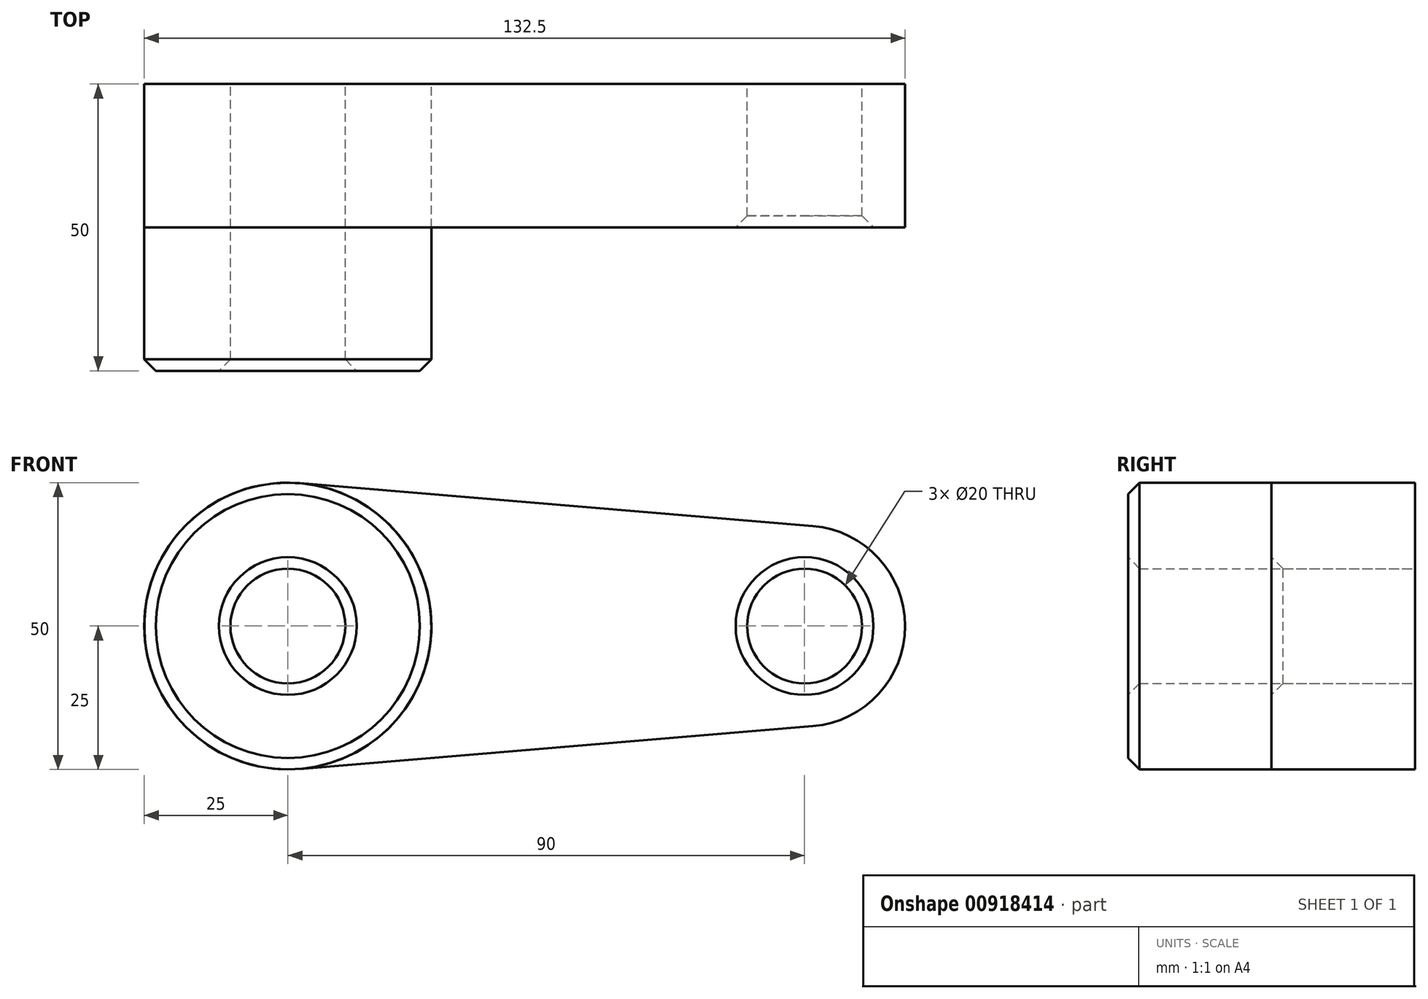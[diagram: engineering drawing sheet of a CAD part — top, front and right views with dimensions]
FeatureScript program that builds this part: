
annotation { "Feature Type Name" : "Feature", "Feature Type Description" : "" }
export const myFeature = defineFeature(function(context is Context, id is Id, definition is map)
    precondition{}
    {
        {
            var Q0;
            Q0=qCreatedBy(makeId("Front.planeOp"),FACE);
            var sketch = newSketch(context, id + "F0", { "sketchPlane" : qUnion([Q0])});
            skCircle(sketch, "E0", {"center": v(0, 0) * mm, "radius": 25 * mm});
            skCircle(sketch, "E1", {"center": v(90, 0) * mm, "radius": 17.5 * mm});
            skLineSegment(sketch, "E2", {"start": v(2.08, 24.91) * mm, "end": v(91.46, 17.44) * mm});
            skLineSegment(sketch, "E3", {"start": v(2.08, -24.91) * mm, "end": v(91.46, -17.44) * mm});
            skCircle(sketch, "E4", {"center": v(0, 0) * mm, "radius": 10 * mm});
            skCircle(sketch, "E5", {"center": v(90, 0) * mm, "radius": 10 * mm});
            skSolve(sketch);
        }
        {
            var Q0;
            Q0=qSketchRegion(id+"F0",true);
            extrude(context, id + "F1", {"entities" : qUnion([Q0]), "depth" : 25 * mm});
        }
        {
            var Q0;
            Q0=makeQuery(id+"F0.imprint","IMPRINT",FACE,{"disambiguationData":[TD([[makeQuery(id+"F0.imprint","IMPRINT",EDGE,{"derivedFrom":sQuery(id+"F0.wireOp",EDGE,"E4")}),-1.0]])]});
            extrude(context, id + "F2", {"entities" : qUnion([Q0]), "operationType" : NewBodyOperationType.ADD, "depth" : 50 * mm});
        }
        {
            var Q0;
            Q0=makeQuery(id+"F2.opExtrude","CAP_EDGE",EDGE,{"disambiguationData":[OSD([sQuery(id+"F0.wireOp",EDGE,"E0")])],"isStart":false});
            var Q1;
            Q1=makeQuery(id+"F2.opExtrude","CAP_EDGE",EDGE,{"disambiguationData":[OSD([sQuery(id+"F0.wireOp",EDGE,"E4")])],"isStart":false});
            var Q2;
            Q2=makeQuery(id+"F1.opExtrude","CAP_EDGE",EDGE,{"disambiguationData":[OSD([sQuery(id+"F0.wireOp",EDGE,"E5")])],"isStart":false});
            chamfer(context, id + "F3", {"entities" : qUnion([Q0, Q1, Q2]), "width" : 2 * mm, "tangentPropagation" : true});
        }
        {
            var Q0;
            Q0=makeQuery(id+"F0.imprint","IMPRINT",FACE,{"disambiguationData":[TD([[makeQuery(id+"F0.imprint","IMPRINT",EDGE,{"derivedFrom":sQuery(id+"F0.wireOp",EDGE,"E4")}),-1.0]])]});
            extrude(context, id + "F4", {"entities" : qUnion([Q0]), "depth" : 25 * mm, "offsetDistance" : 25 * mm});
        }
    });
